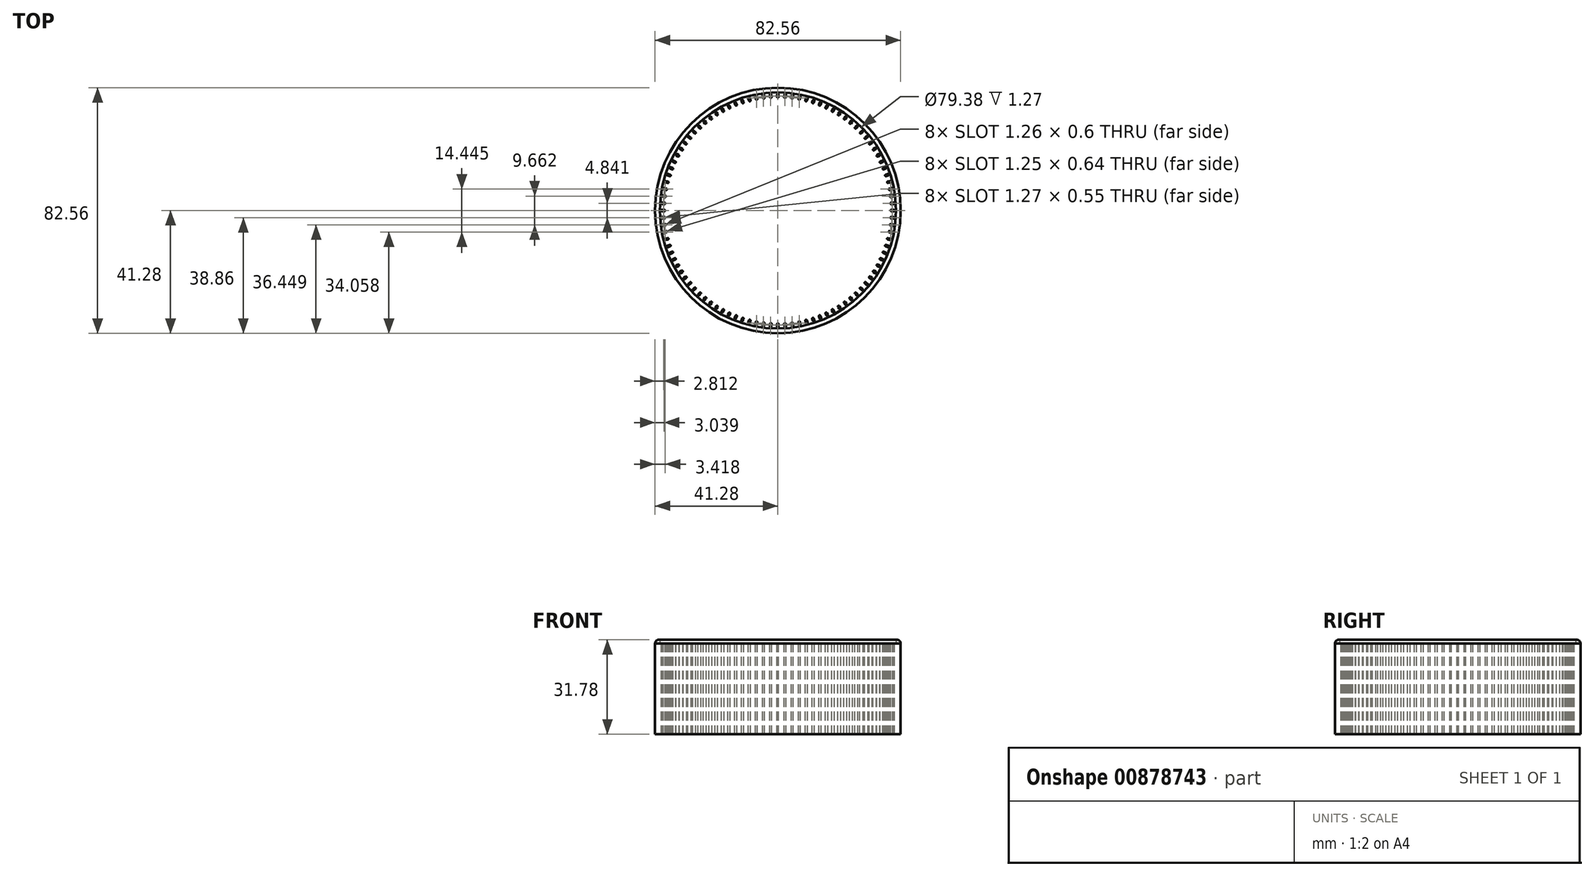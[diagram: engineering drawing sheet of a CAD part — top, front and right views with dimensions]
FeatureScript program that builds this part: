
annotation { "Feature Type Name" : "Feature", "Feature Type Description" : "" }
export const myFeature = defineFeature(function(context is Context, id is Id, definition is map)
    precondition{}
    {
        {
            var Q0;
            Q0=qCreatedBy(makeId("Top.planeOp"),FACE);
            var sketch = newSketch(context, id + "F0", { "sketchPlane" : qUnion([Q0])});
            skCircle(sketch, "E0", {"center": v(0, 0) * mm, "radius": 41.28 * mm});
            skSolve(sketch);
        }
        {
            var Q0;
            Q0 = qSketchRegion(id + "F0", true);
            extrude(context, id + "F1", {"entities" : qUnion([Q0]), "depth" : 30.48 * mm, "offsetDistance" : 25.4 * mm});
        }
        {
            var Q0;
            Q0=makeQuery(id+"F1.opExtrude","CAP_FACE",FACE,{"disambiguationData":[OSD([sQuery(id+"F0.wireOp",EDGE,"E0")])],"isStart":false});
            var sketch = newSketch(context, id + "F2", { "sketchPlane" : qUnion([Q0])});
            skCircle(sketch, "E1", {"center": v(0, 0) * mm, "radius": 39.69 * mm});
            skSolve(sketch);
        }
        {
            var Q0;
            Q0 = qSketchRegion(id + "F2", true);
            extrude(context, id + "F3", {"entities" : qUnion([Q0]), "operationType" : NewBodyOperationType.ADD, "depth" : 1.27 * mm, "offsetDistance" : 25.4 * mm});
        }
        {
            var Q0;
            Q0=qCreatedBy(makeId("Right.planeOp"),FACE);
            var sketch = newSketch(context, id + "F4", { "sketchPlane" : qUnion([Q0])});
            skLineSegment(sketch, "E2.0", {"start": v(-39.69, 31.75) * mm, "end": v(39.69, 31.75) * mm, "construction": true});
            skLineSegment(sketch, "E3.0", {"start": v(-41.28, 30.48) * mm, "end": v(41.28, 30.48) * mm, "construction": true});
            skArc(sketch, "E4", {"start": v(-39.69, 31.75) * mm, "mid": v(-40.79, 31.5) * mm, "end": v(-41.28, 30.48) * mm});
            skLineSegment(sketch, "E5", {"start": v(-39.69, 31.75) * mm, "end": v(-39.69, 30.48) * mm});
            skLineSegment(sketch, "E6", {"start": v(-39.69, 30.48) * mm, "end": v(-41.28, 30.48) * mm});
            skSolve(sketch);
        }
        {
            var Q0;
            Q0=qCreatedBy(makeId("Front.planeOp"),FACE);
            var sketch = newSketch(context, id + "F5", { "sketchPlane" : qUnion([Q0])});
            skLineSegment(sketch, "E7", {"start": v(0, 0) * mm, "end": v(0, 34.96) * mm});
            skSolve(sketch);
        }
        {
            var Q0;
            Q0 = qSketchRegion(id + "F4", true);
            var Q1;
            Q1=sQuery(id+"F5.wireOp",EDGE,"E7");
            revolve(context, id + "F6", {"surfaceOperationType" : NewSurfaceOperationType.NEW, "entities" : qUnion([Q0]), "axis" : qUnion([Q1]), "revolveType" : RevolveType.FULL});
        }
        {
            var Q0;
            Q0=makeQuery(id+"F3.opExtrude","CAP_FACE",FACE,{"disambiguationData":[OSD([sQuery(id+"F2.wireOp",EDGE,"E1")])],"isStart":false});
            var sketch = newSketch(context, id + "F7", { "sketchPlane" : qUnion([Q0])});
            skCircle(sketch, "E8", {"center": v(0, 0) * mm, "radius": 39.18 * mm, "construction": true});
            skLineSegment(sketch, "E9.bottom", {"start": v(-0.25, 38.93) * mm, "end": v(0.25, 38.93) * mm, "construction": true});
            skLineSegment(sketch, "E9.top", {"start": v(-0.25, 38.16) * mm, "end": v(0.25, 38.16) * mm, "construction": true});
            skLineSegment(sketch, "E9.left", {"start": v(-0.25, 38.93) * mm, "end": v(-0.25, 38.16) * mm});
            skLineSegment(sketch, "E9.right", {"start": v(0.25, 38.93) * mm, "end": v(0.25, 38.16) * mm});
            skArc(sketch, "E10", {"start": v(0.25, 38.93) * mm, "mid": v(0, 39.18) * mm, "end": v(-0.25, 38.93) * mm});
            skArc(sketch, "E11", {"start": v(-0.25, 38.16) * mm, "mid": v(0, 37.9) * mm, "end": v(0.25, 38.16) * mm});
            skArc(sketch, "E12.1.0", {"start": v(-2.2, 38.86) * mm, "mid": v(-2.46, 39.1) * mm, "end": v(-2.7, 38.83) * mm});
            skLineSegment(sketch, "E12.1.1", {"start": v(-2.2, 38.86) * mm, "end": v(-2.14, 38.1) * mm});
            skArc(sketch, "E12.1.2", {"start": v(-2.65, 38.07) * mm, "mid": v(-2.38, 37.83) * mm, "end": v(-2.14, 38.1) * mm});
            skLineSegment(sketch, "E12.1.3", {"start": v(-2.7, 38.83) * mm, "end": v(-2.65, 38.07) * mm});
            skArc(sketch, "E12.2.0", {"start": v(-4.63, 38.65) * mm, "mid": v(-4.91, 38.87) * mm, "end": v(-5.13, 38.59) * mm});
            skLineSegment(sketch, "E12.2.1", {"start": v(-4.63, 38.65) * mm, "end": v(-4.53, 37.9) * mm});
            skArc(sketch, "E12.2.2", {"start": v(-5.04, 37.83) * mm, "mid": v(-4.75, 37.61) * mm, "end": v(-4.53, 37.9) * mm});
            skLineSegment(sketch, "E12.2.3", {"start": v(-5.13, 38.59) * mm, "end": v(-5.04, 37.83) * mm});
            skArc(sketch, "E12.3.0", {"start": v(-7.04, 38.28) * mm, "mid": v(-7.34, 38.49) * mm, "end": v(-7.54, 38.19) * mm});
            skLineSegment(sketch, "E12.3.1", {"start": v(-7.04, 38.28) * mm, "end": v(-6.9, 37.54) * mm});
            skArc(sketch, "E12.3.2", {"start": v(-7.4, 37.44) * mm, "mid": v(-7.1, 37.24) * mm, "end": v(-6.9, 37.54) * mm});
            skLineSegment(sketch, "E12.3.3", {"start": v(-7.54, 38.19) * mm, "end": v(-7.4, 37.44) * mm});
            skArc(sketch, "E12.4.0", {"start": v(-9.43, 37.77) * mm, "mid": v(-9.74, 37.95) * mm, "end": v(-9.93, 37.64) * mm});
            skLineSegment(sketch, "E12.4.1", {"start": v(-9.43, 37.77) * mm, "end": v(-9.24, 37.03) * mm});
            skArc(sketch, "E12.4.2", {"start": v(-9.74, 36.9) * mm, "mid": v(-9.43, 36.72) * mm, "end": v(-9.24, 37.03) * mm});
            skLineSegment(sketch, "E12.4.3", {"start": v(-9.93, 37.64) * mm, "end": v(-9.74, 36.9) * mm});
            skArc(sketch, "E12.5.0", {"start": v(-11.79, 37.1) * mm, "mid": v(-12.1, 37.26) * mm, "end": v(-12.27, 36.94) * mm});
            skLineSegment(sketch, "E12.5.1", {"start": v(-11.79, 37.1) * mm, "end": v(-11.55, 36.37) * mm});
            skArc(sketch, "E12.5.2", {"start": v(-12.03, 36.22) * mm, "mid": v(-11.71, 36.05) * mm, "end": v(-11.55, 36.37) * mm});
            skLineSegment(sketch, "E12.5.3", {"start": v(-12.27, 36.94) * mm, "end": v(-12.03, 36.22) * mm});
            skArc(sketch, "E12.6.0", {"start": v(-14.1, 36.29) * mm, "mid": v(-14.42, 36.43) * mm, "end": v(-14.57, 36.1) * mm});
            skLineSegment(sketch, "E12.6.1", {"start": v(-14.1, 36.29) * mm, "end": v(-13.81, 35.58) * mm});
            skArc(sketch, "E12.6.2", {"start": v(-14.29, 35.4) * mm, "mid": v(-13.96, 35.25) * mm, "end": v(-13.81, 35.58) * mm});
            skLineSegment(sketch, "E12.6.3", {"start": v(-14.57, 36.1) * mm, "end": v(-14.29, 35.4) * mm});
            skArc(sketch, "E12.7.0", {"start": v(-16.34, 35.33) * mm, "mid": v(-16.68, 35.45) * mm, "end": v(-16.8, 35.11) * mm});
            skLineSegment(sketch, "E12.7.1", {"start": v(-16.34, 35.33) * mm, "end": v(-16.02, 34.64) * mm});
            skArc(sketch, "E12.7.2", {"start": v(-16.48, 34.42) * mm, "mid": v(-16.14, 34.3) * mm, "end": v(-16.02, 34.64) * mm});
            skLineSegment(sketch, "E12.7.3", {"start": v(-16.8, 35.11) * mm, "end": v(-16.48, 34.42) * mm});
            skArc(sketch, "E12.8.0", {"start": v(-18.53, 34.23) * mm, "mid": v(-18.87, 34.33) * mm, "end": v(-18.98, 33.99) * mm});
            skLineSegment(sketch, "E12.8.1", {"start": v(-18.53, 34.23) * mm, "end": v(-18.16, 33.57) * mm});
            skArc(sketch, "E12.8.2", {"start": v(-18.6, 33.32) * mm, "mid": v(-18.26, 33.22) * mm, "end": v(-18.16, 33.57) * mm});
            skLineSegment(sketch, "E12.8.3", {"start": v(-18.98, 33.99) * mm, "end": v(-18.6, 33.32) * mm});
            skArc(sketch, "E12.9.0", {"start": v(-20.64, 33) * mm, "mid": v(-21, 33.08) * mm, "end": v(-21.07, 32.73) * mm});
            skLineSegment(sketch, "E12.9.1", {"start": v(-20.64, 33) * mm, "end": v(-20.23, 32.36) * mm});
            skArc(sketch, "E12.9.2", {"start": v(-20.66, 32.09) * mm, "mid": v(-20.31, 32) * mm, "end": v(-20.23, 32.36) * mm});
            skLineSegment(sketch, "E12.9.3", {"start": v(-21.07, 32.73) * mm, "end": v(-20.66, 32.09) * mm});
            skArc(sketch, "E12.10.0", {"start": v(-22.67, 31.64) * mm, "mid": v(-23.03, 31.7) * mm, "end": v(-23.09, 31.34) * mm});
            skLineSegment(sketch, "E12.10.1", {"start": v(-22.67, 31.64) * mm, "end": v(-22.23, 31.02) * mm});
            skArc(sketch, "E12.10.2", {"start": v(-22.64, 30.73) * mm, "mid": v(-22.28, 30.67) * mm, "end": v(-22.23, 31.02) * mm});
            skLineSegment(sketch, "E12.10.3", {"start": v(-23.09, 31.34) * mm, "end": v(-22.64, 30.73) * mm});
            skArc(sketch, "E12.11.0", {"start": v(-24.62, 30.15) * mm, "mid": v(-24.97, 30.19) * mm, "end": v(-25, 29.83) * mm});
            skLineSegment(sketch, "E12.11.1", {"start": v(-24.62, 30.15) * mm, "end": v(-24.13, 29.57) * mm});
            skArc(sketch, "E12.11.2", {"start": v(-24.52, 29.24) * mm, "mid": v(-24.16, 29.2) * mm, "end": v(-24.13, 29.57) * mm});
            skLineSegment(sketch, "E12.11.3", {"start": v(-25, 29.83) * mm, "end": v(-24.52, 29.24) * mm});
            skArc(sketch, "E12.12.0", {"start": v(-26.46, 28.55) * mm, "mid": v(-26.82, 28.56) * mm, "end": v(-26.83, 28.2) * mm});
            skLineSegment(sketch, "E12.12.1", {"start": v(-26.46, 28.55) * mm, "end": v(-25.94, 28) * mm});
            skArc(sketch, "E12.12.2", {"start": v(-26.3, 27.65) * mm, "mid": v(-25.95, 27.63) * mm, "end": v(-25.94, 28) * mm});
            skLineSegment(sketch, "E12.12.3", {"start": v(-26.83, 28.2) * mm, "end": v(-26.3, 27.65) * mm});
            skArc(sketch, "E12.13.0", {"start": v(-28.2, 26.83) * mm, "mid": v(-28.56, 26.82) * mm, "end": v(-28.55, 26.46) * mm});
            skLineSegment(sketch, "E12.13.1", {"start": v(-28.2, 26.83) * mm, "end": v(-27.65, 26.3) * mm});
            skArc(sketch, "E12.13.2", {"start": v(-28, 25.94) * mm, "mid": v(-27.63, 25.95) * mm, "end": v(-27.65, 26.3) * mm});
            skLineSegment(sketch, "E12.13.3", {"start": v(-28.55, 26.46) * mm, "end": v(-28, 25.94) * mm});
            skArc(sketch, "E12.14.0", {"start": v(-29.83, 25) * mm, "mid": v(-30.19, 24.97) * mm, "end": v(-30.15, 24.62) * mm});
            skLineSegment(sketch, "E12.14.1", {"start": v(-29.83, 25) * mm, "end": v(-29.24, 24.52) * mm});
            skArc(sketch, "E12.14.2", {"start": v(-29.57, 24.13) * mm, "mid": v(-29.2, 24.16) * mm, "end": v(-29.24, 24.52) * mm});
            skLineSegment(sketch, "E12.14.3", {"start": v(-30.15, 24.62) * mm, "end": v(-29.57, 24.13) * mm});
            skArc(sketch, "E12.15.0", {"start": v(-31.34, 23.09) * mm, "mid": v(-31.7, 23.03) * mm, "end": v(-31.64, 22.67) * mm});
            skLineSegment(sketch, "E12.15.1", {"start": v(-31.34, 23.09) * mm, "end": v(-30.73, 22.64) * mm});
            skArc(sketch, "E12.15.2", {"start": v(-31.02, 22.23) * mm, "mid": v(-30.67, 22.28) * mm, "end": v(-30.73, 22.64) * mm});
            skLineSegment(sketch, "E12.15.3", {"start": v(-31.64, 22.67) * mm, "end": v(-31.02, 22.23) * mm});
            skArc(sketch, "E12.16.0", {"start": v(-32.73, 21.07) * mm, "mid": v(-33.08, 21) * mm, "end": v(-33, 20.64) * mm});
            skLineSegment(sketch, "E12.16.1", {"start": v(-32.73, 21.07) * mm, "end": v(-32.09, 20.66) * mm});
            skArc(sketch, "E12.16.2", {"start": v(-32.36, 20.23) * mm, "mid": v(-32, 20.31) * mm, "end": v(-32.09, 20.66) * mm});
            skLineSegment(sketch, "E12.16.3", {"start": v(-33, 20.64) * mm, "end": v(-32.36, 20.23) * mm});
            skArc(sketch, "E12.17.0", {"start": v(-33.99, 18.98) * mm, "mid": v(-34.33, 18.87) * mm, "end": v(-34.23, 18.53) * mm});
            skLineSegment(sketch, "E12.17.1", {"start": v(-33.99, 18.98) * mm, "end": v(-33.32, 18.6) * mm});
            skArc(sketch, "E12.17.2", {"start": v(-33.57, 18.16) * mm, "mid": v(-33.22, 18.26) * mm, "end": v(-33.32, 18.6) * mm});
            skLineSegment(sketch, "E12.17.3", {"start": v(-34.23, 18.53) * mm, "end": v(-33.57, 18.16) * mm});
            skArc(sketch, "E12.18.0", {"start": v(-35.11, 16.8) * mm, "mid": v(-35.45, 16.68) * mm, "end": v(-35.33, 16.34) * mm});
            skLineSegment(sketch, "E12.18.1", {"start": v(-35.11, 16.8) * mm, "end": v(-34.42, 16.48) * mm});
            skArc(sketch, "E12.18.2", {"start": v(-34.64, 16.02) * mm, "mid": v(-34.3, 16.14) * mm, "end": v(-34.42, 16.48) * mm});
            skLineSegment(sketch, "E12.18.3", {"start": v(-35.33, 16.34) * mm, "end": v(-34.64, 16.02) * mm});
            skArc(sketch, "E12.19.0", {"start": v(-36.1, 14.57) * mm, "mid": v(-36.43, 14.42) * mm, "end": v(-36.29, 14.1) * mm});
            skLineSegment(sketch, "E12.19.1", {"start": v(-36.1, 14.57) * mm, "end": v(-35.4, 14.29) * mm});
            skArc(sketch, "E12.19.2", {"start": v(-35.58, 13.81) * mm, "mid": v(-35.25, 13.96) * mm, "end": v(-35.4, 14.29) * mm});
            skLineSegment(sketch, "E12.19.3", {"start": v(-36.29, 14.1) * mm, "end": v(-35.58, 13.81) * mm});
            skArc(sketch, "E12.20.0", {"start": v(-36.94, 12.27) * mm, "mid": v(-37.26, 12.1) * mm, "end": v(-37.1, 11.79) * mm});
            skLineSegment(sketch, "E12.20.1", {"start": v(-36.94, 12.27) * mm, "end": v(-36.22, 12.03) * mm});
            skArc(sketch, "E12.20.2", {"start": v(-36.37, 11.55) * mm, "mid": v(-36.05, 11.71) * mm, "end": v(-36.22, 12.03) * mm});
            skLineSegment(sketch, "E12.20.3", {"start": v(-37.1, 11.79) * mm, "end": v(-36.37, 11.55) * mm});
            skArc(sketch, "E12.21.0", {"start": v(-37.64, 9.93) * mm, "mid": v(-37.95, 9.74) * mm, "end": v(-37.77, 9.43) * mm});
            skLineSegment(sketch, "E12.21.1", {"start": v(-37.64, 9.93) * mm, "end": v(-36.9, 9.74) * mm});
            skArc(sketch, "E12.21.2", {"start": v(-37.03, 9.24) * mm, "mid": v(-36.72, 9.43) * mm, "end": v(-36.9, 9.74) * mm});
            skLineSegment(sketch, "E12.21.3", {"start": v(-37.77, 9.43) * mm, "end": v(-37.03, 9.24) * mm});
            skArc(sketch, "E12.22.0", {"start": v(-38.19, 7.54) * mm, "mid": v(-38.49, 7.34) * mm, "end": v(-38.28, 7.04) * mm});
            skLineSegment(sketch, "E12.22.1", {"start": v(-38.19, 7.54) * mm, "end": v(-37.44, 7.4) * mm});
            skArc(sketch, "E12.22.2", {"start": v(-37.54, 6.9) * mm, "mid": v(-37.24, 7.1) * mm, "end": v(-37.44, 7.4) * mm});
            skLineSegment(sketch, "E12.22.3", {"start": v(-38.28, 7.04) * mm, "end": v(-37.54, 6.9) * mm});
            skArc(sketch, "E12.23.0", {"start": v(-38.59, 5.13) * mm, "mid": v(-38.87, 4.91) * mm, "end": v(-38.65, 4.63) * mm});
            skLineSegment(sketch, "E12.23.1", {"start": v(-38.59, 5.13) * mm, "end": v(-37.83, 5.04) * mm});
            skArc(sketch, "E12.23.2", {"start": v(-37.9, 4.53) * mm, "mid": v(-37.61, 4.75) * mm, "end": v(-37.83, 5.04) * mm});
            skLineSegment(sketch, "E12.23.3", {"start": v(-38.65, 4.63) * mm, "end": v(-37.9, 4.53) * mm});
            skArc(sketch, "E12.24.0", {"start": v(-38.83, 2.7) * mm, "mid": v(-39.1, 2.46) * mm, "end": v(-38.86, 2.2) * mm});
            skLineSegment(sketch, "E12.24.1", {"start": v(-38.83, 2.7) * mm, "end": v(-38.07, 2.65) * mm});
            skArc(sketch, "E12.24.2", {"start": v(-38.1, 2.14) * mm, "mid": v(-37.83, 2.38) * mm, "end": v(-38.07, 2.65) * mm});
            skLineSegment(sketch, "E12.24.3", {"start": v(-38.86, 2.2) * mm, "end": v(-38.1, 2.14) * mm});
            skArc(sketch, "E12.25.0", {"start": v(-38.93, 0.25) * mm, "mid": v(-39.18, 0) * mm, "end": v(-38.93, -0.25) * mm});
            skLineSegment(sketch, "E12.25.1", {"start": v(-38.93, 0.25) * mm, "end": v(-38.16, 0.25) * mm});
            skArc(sketch, "E12.25.2", {"start": v(-38.16, -0.25) * mm, "mid": v(-37.9, 0) * mm, "end": v(-38.16, 0.25) * mm});
            skLineSegment(sketch, "E12.25.3", {"start": v(-38.93, -0.25) * mm, "end": v(-38.16, -0.25) * mm});
            skArc(sketch, "E12.26.0", {"start": v(-38.86, -2.2) * mm, "mid": v(-39.1, -2.46) * mm, "end": v(-38.83, -2.7) * mm});
            skLineSegment(sketch, "E12.26.1", {"start": v(-38.86, -2.2) * mm, "end": v(-38.1, -2.14) * mm});
            skArc(sketch, "E12.26.2", {"start": v(-38.07, -2.65) * mm, "mid": v(-37.83, -2.38) * mm, "end": v(-38.1, -2.14) * mm});
            skLineSegment(sketch, "E12.26.3", {"start": v(-38.83, -2.7) * mm, "end": v(-38.07, -2.65) * mm});
            skArc(sketch, "E12.27.0", {"start": v(-38.65, -4.63) * mm, "mid": v(-38.87, -4.91) * mm, "end": v(-38.59, -5.13) * mm});
            skLineSegment(sketch, "E12.27.1", {"start": v(-38.65, -4.63) * mm, "end": v(-37.9, -4.53) * mm});
            skArc(sketch, "E12.27.2", {"start": v(-37.83, -5.04) * mm, "mid": v(-37.61, -4.75) * mm, "end": v(-37.9, -4.53) * mm});
            skLineSegment(sketch, "E12.27.3", {"start": v(-38.59, -5.13) * mm, "end": v(-37.83, -5.04) * mm});
            skArc(sketch, "E12.28.0", {"start": v(-38.28, -7.04) * mm, "mid": v(-38.49, -7.34) * mm, "end": v(-38.19, -7.54) * mm});
            skLineSegment(sketch, "E12.28.1", {"start": v(-38.28, -7.04) * mm, "end": v(-37.54, -6.9) * mm});
            skArc(sketch, "E12.28.2", {"start": v(-37.44, -7.4) * mm, "mid": v(-37.24, -7.1) * mm, "end": v(-37.54, -6.9) * mm});
            skLineSegment(sketch, "E12.28.3", {"start": v(-38.19, -7.54) * mm, "end": v(-37.44, -7.4) * mm});
            skArc(sketch, "E12.29.0", {"start": v(-37.77, -9.43) * mm, "mid": v(-37.95, -9.74) * mm, "end": v(-37.64, -9.93) * mm});
            skLineSegment(sketch, "E12.29.1", {"start": v(-37.77, -9.43) * mm, "end": v(-37.03, -9.24) * mm});
            skArc(sketch, "E12.29.2", {"start": v(-36.9, -9.74) * mm, "mid": v(-36.72, -9.43) * mm, "end": v(-37.03, -9.24) * mm});
            skLineSegment(sketch, "E12.29.3", {"start": v(-37.64, -9.93) * mm, "end": v(-36.9, -9.74) * mm});
            skArc(sketch, "E12.30.0", {"start": v(-37.1, -11.79) * mm, "mid": v(-37.26, -12.1) * mm, "end": v(-36.94, -12.27) * mm});
            skLineSegment(sketch, "E12.30.1", {"start": v(-37.1, -11.79) * mm, "end": v(-36.37, -11.55) * mm});
            skArc(sketch, "E12.30.2", {"start": v(-36.22, -12.03) * mm, "mid": v(-36.05, -11.71) * mm, "end": v(-36.37, -11.55) * mm});
            skLineSegment(sketch, "E12.30.3", {"start": v(-36.94, -12.27) * mm, "end": v(-36.22, -12.03) * mm});
            skArc(sketch, "E12.31.0", {"start": v(-36.29, -14.1) * mm, "mid": v(-36.43, -14.42) * mm, "end": v(-36.1, -14.57) * mm});
            skLineSegment(sketch, "E12.31.1", {"start": v(-36.29, -14.1) * mm, "end": v(-35.58, -13.81) * mm});
            skArc(sketch, "E12.31.2", {"start": v(-35.4, -14.29) * mm, "mid": v(-35.25, -13.96) * mm, "end": v(-35.58, -13.81) * mm});
            skLineSegment(sketch, "E12.31.3", {"start": v(-36.1, -14.57) * mm, "end": v(-35.4, -14.29) * mm});
            skArc(sketch, "E12.32.0", {"start": v(-35.33, -16.34) * mm, "mid": v(-35.45, -16.68) * mm, "end": v(-35.11, -16.8) * mm});
            skLineSegment(sketch, "E12.32.1", {"start": v(-35.33, -16.34) * mm, "end": v(-34.64, -16.02) * mm});
            skArc(sketch, "E12.32.2", {"start": v(-34.42, -16.48) * mm, "mid": v(-34.3, -16.14) * mm, "end": v(-34.64, -16.02) * mm});
            skLineSegment(sketch, "E12.32.3", {"start": v(-35.11, -16.8) * mm, "end": v(-34.42, -16.48) * mm});
            skArc(sketch, "E12.33.0", {"start": v(-34.23, -18.53) * mm, "mid": v(-34.33, -18.87) * mm, "end": v(-33.99, -18.98) * mm});
            skLineSegment(sketch, "E12.33.1", {"start": v(-34.23, -18.53) * mm, "end": v(-33.57, -18.16) * mm});
            skArc(sketch, "E12.33.2", {"start": v(-33.32, -18.6) * mm, "mid": v(-33.22, -18.26) * mm, "end": v(-33.57, -18.16) * mm});
            skLineSegment(sketch, "E12.33.3", {"start": v(-33.99, -18.98) * mm, "end": v(-33.32, -18.6) * mm});
            skArc(sketch, "E12.34.0", {"start": v(-33, -20.64) * mm, "mid": v(-33.08, -21) * mm, "end": v(-32.73, -21.07) * mm});
            skLineSegment(sketch, "E12.34.1", {"start": v(-33, -20.64) * mm, "end": v(-32.36, -20.23) * mm});
            skArc(sketch, "E12.34.2", {"start": v(-32.09, -20.66) * mm, "mid": v(-32, -20.31) * mm, "end": v(-32.36, -20.23) * mm});
            skLineSegment(sketch, "E12.34.3", {"start": v(-32.73, -21.07) * mm, "end": v(-32.09, -20.66) * mm});
            skArc(sketch, "E12.35.0", {"start": v(-31.64, -22.67) * mm, "mid": v(-31.7, -23.03) * mm, "end": v(-31.34, -23.09) * mm});
            skLineSegment(sketch, "E12.35.1", {"start": v(-31.64, -22.67) * mm, "end": v(-31.02, -22.23) * mm});
            skArc(sketch, "E12.35.2", {"start": v(-30.73, -22.64) * mm, "mid": v(-30.67, -22.28) * mm, "end": v(-31.02, -22.23) * mm});
            skLineSegment(sketch, "E12.35.3", {"start": v(-31.34, -23.09) * mm, "end": v(-30.73, -22.64) * mm});
            skArc(sketch, "E12.36.0", {"start": v(-30.15, -24.62) * mm, "mid": v(-30.19, -24.97) * mm, "end": v(-29.83, -25) * mm});
            skLineSegment(sketch, "E12.36.1", {"start": v(-30.15, -24.62) * mm, "end": v(-29.57, -24.13) * mm});
            skArc(sketch, "E12.36.2", {"start": v(-29.24, -24.52) * mm, "mid": v(-29.2, -24.16) * mm, "end": v(-29.57, -24.13) * mm});
            skLineSegment(sketch, "E12.36.3", {"start": v(-29.83, -25) * mm, "end": v(-29.24, -24.52) * mm});
            skArc(sketch, "E12.37.0", {"start": v(-28.55, -26.46) * mm, "mid": v(-28.56, -26.82) * mm, "end": v(-28.2, -26.83) * mm});
            skLineSegment(sketch, "E12.37.1", {"start": v(-28.55, -26.46) * mm, "end": v(-28, -25.94) * mm});
            skArc(sketch, "E12.37.2", {"start": v(-27.65, -26.3) * mm, "mid": v(-27.63, -25.95) * mm, "end": v(-28, -25.94) * mm});
            skLineSegment(sketch, "E12.37.3", {"start": v(-28.2, -26.83) * mm, "end": v(-27.65, -26.3) * mm});
            skArc(sketch, "E12.38.0", {"start": v(-26.83, -28.2) * mm, "mid": v(-26.82, -28.56) * mm, "end": v(-26.46, -28.55) * mm});
            skLineSegment(sketch, "E12.38.1", {"start": v(-26.83, -28.2) * mm, "end": v(-26.3, -27.65) * mm});
            skArc(sketch, "E12.38.2", {"start": v(-25.94, -28) * mm, "mid": v(-25.95, -27.63) * mm, "end": v(-26.3, -27.65) * mm});
            skLineSegment(sketch, "E12.38.3", {"start": v(-26.46, -28.55) * mm, "end": v(-25.94, -28) * mm});
            skArc(sketch, "E12.39.0", {"start": v(-25, -29.83) * mm, "mid": v(-24.97, -30.19) * mm, "end": v(-24.62, -30.15) * mm});
            skLineSegment(sketch, "E12.39.1", {"start": v(-25, -29.83) * mm, "end": v(-24.52, -29.24) * mm});
            skArc(sketch, "E12.39.2", {"start": v(-24.13, -29.57) * mm, "mid": v(-24.16, -29.2) * mm, "end": v(-24.52, -29.24) * mm});
            skLineSegment(sketch, "E12.39.3", {"start": v(-24.62, -30.15) * mm, "end": v(-24.13, -29.57) * mm});
            skArc(sketch, "E12.40.0", {"start": v(-23.09, -31.34) * mm, "mid": v(-23.03, -31.7) * mm, "end": v(-22.67, -31.64) * mm});
            skLineSegment(sketch, "E12.40.1", {"start": v(-23.09, -31.34) * mm, "end": v(-22.64, -30.73) * mm});
            skArc(sketch, "E12.40.2", {"start": v(-22.23, -31.02) * mm, "mid": v(-22.28, -30.67) * mm, "end": v(-22.64, -30.73) * mm});
            skLineSegment(sketch, "E12.40.3", {"start": v(-22.67, -31.64) * mm, "end": v(-22.23, -31.02) * mm});
            skArc(sketch, "E12.41.0", {"start": v(-21.07, -32.73) * mm, "mid": v(-21, -33.08) * mm, "end": v(-20.64, -33) * mm});
            skLineSegment(sketch, "E12.41.1", {"start": v(-21.07, -32.73) * mm, "end": v(-20.66, -32.09) * mm});
            skArc(sketch, "E12.41.2", {"start": v(-20.23, -32.36) * mm, "mid": v(-20.31, -32) * mm, "end": v(-20.66, -32.09) * mm});
            skLineSegment(sketch, "E12.41.3", {"start": v(-20.64, -33) * mm, "end": v(-20.23, -32.36) * mm});
            skArc(sketch, "E12.42.0", {"start": v(-18.98, -33.99) * mm, "mid": v(-18.87, -34.33) * mm, "end": v(-18.53, -34.23) * mm});
            skLineSegment(sketch, "E12.42.1", {"start": v(-18.98, -33.99) * mm, "end": v(-18.6, -33.32) * mm});
            skArc(sketch, "E12.42.2", {"start": v(-18.16, -33.57) * mm, "mid": v(-18.26, -33.22) * mm, "end": v(-18.6, -33.32) * mm});
            skLineSegment(sketch, "E12.42.3", {"start": v(-18.53, -34.23) * mm, "end": v(-18.16, -33.57) * mm});
            skArc(sketch, "E12.43.0", {"start": v(-16.8, -35.11) * mm, "mid": v(-16.68, -35.45) * mm, "end": v(-16.34, -35.33) * mm});
            skLineSegment(sketch, "E12.43.1", {"start": v(-16.8, -35.11) * mm, "end": v(-16.48, -34.42) * mm});
            skArc(sketch, "E12.43.2", {"start": v(-16.02, -34.64) * mm, "mid": v(-16.14, -34.3) * mm, "end": v(-16.48, -34.42) * mm});
            skLineSegment(sketch, "E12.43.3", {"start": v(-16.34, -35.33) * mm, "end": v(-16.02, -34.64) * mm});
            skArc(sketch, "E12.44.0", {"start": v(-14.57, -36.1) * mm, "mid": v(-14.42, -36.43) * mm, "end": v(-14.1, -36.29) * mm});
            skLineSegment(sketch, "E12.44.1", {"start": v(-14.57, -36.1) * mm, "end": v(-14.29, -35.4) * mm});
            skArc(sketch, "E12.44.2", {"start": v(-13.81, -35.58) * mm, "mid": v(-13.96, -35.25) * mm, "end": v(-14.29, -35.4) * mm});
            skLineSegment(sketch, "E12.44.3", {"start": v(-14.1, -36.29) * mm, "end": v(-13.81, -35.58) * mm});
            skArc(sketch, "E12.45.0", {"start": v(-12.27, -36.94) * mm, "mid": v(-12.1, -37.26) * mm, "end": v(-11.79, -37.1) * mm});
            skLineSegment(sketch, "E12.45.1", {"start": v(-12.27, -36.94) * mm, "end": v(-12.03, -36.22) * mm});
            skArc(sketch, "E12.45.2", {"start": v(-11.55, -36.37) * mm, "mid": v(-11.71, -36.05) * mm, "end": v(-12.03, -36.22) * mm});
            skLineSegment(sketch, "E12.45.3", {"start": v(-11.79, -37.1) * mm, "end": v(-11.55, -36.37) * mm});
            skArc(sketch, "E12.46.0", {"start": v(-9.93, -37.64) * mm, "mid": v(-9.74, -37.95) * mm, "end": v(-9.43, -37.77) * mm});
            skLineSegment(sketch, "E12.46.1", {"start": v(-9.93, -37.64) * mm, "end": v(-9.74, -36.9) * mm});
            skArc(sketch, "E12.46.2", {"start": v(-9.24, -37.03) * mm, "mid": v(-9.43, -36.72) * mm, "end": v(-9.74, -36.9) * mm});
            skLineSegment(sketch, "E12.46.3", {"start": v(-9.43, -37.77) * mm, "end": v(-9.24, -37.03) * mm});
            skArc(sketch, "E12.47.0", {"start": v(-7.54, -38.19) * mm, "mid": v(-7.34, -38.49) * mm, "end": v(-7.04, -38.28) * mm});
            skLineSegment(sketch, "E12.47.1", {"start": v(-7.54, -38.19) * mm, "end": v(-7.4, -37.44) * mm});
            skArc(sketch, "E12.47.2", {"start": v(-6.9, -37.54) * mm, "mid": v(-7.1, -37.24) * mm, "end": v(-7.4, -37.44) * mm});
            skLineSegment(sketch, "E12.47.3", {"start": v(-7.04, -38.28) * mm, "end": v(-6.9, -37.54) * mm});
            skArc(sketch, "E12.48.0", {"start": v(-5.13, -38.59) * mm, "mid": v(-4.91, -38.87) * mm, "end": v(-4.63, -38.65) * mm});
            skLineSegment(sketch, "E12.48.1", {"start": v(-5.13, -38.59) * mm, "end": v(-5.04, -37.83) * mm});
            skArc(sketch, "E12.48.2", {"start": v(-4.53, -37.9) * mm, "mid": v(-4.75, -37.61) * mm, "end": v(-5.04, -37.83) * mm});
            skLineSegment(sketch, "E12.48.3", {"start": v(-4.63, -38.65) * mm, "end": v(-4.53, -37.9) * mm});
            skArc(sketch, "E12.49.0", {"start": v(-2.7, -38.83) * mm, "mid": v(-2.46, -39.1) * mm, "end": v(-2.2, -38.86) * mm});
            skLineSegment(sketch, "E12.49.1", {"start": v(-2.7, -38.83) * mm, "end": v(-2.65, -38.07) * mm});
            skArc(sketch, "E12.49.2", {"start": v(-2.14, -38.1) * mm, "mid": v(-2.38, -37.83) * mm, "end": v(-2.65, -38.07) * mm});
            skLineSegment(sketch, "E12.49.3", {"start": v(-2.2, -38.86) * mm, "end": v(-2.14, -38.1) * mm});
            skArc(sketch, "E12.50.0", {"start": v(-0.25, -38.93) * mm, "mid": v(0, -39.18) * mm, "end": v(0.25, -38.93) * mm});
            skLineSegment(sketch, "E12.50.1", {"start": v(-0.25, -38.93) * mm, "end": v(-0.25, -38.16) * mm});
            skArc(sketch, "E12.50.2", {"start": v(0.25, -38.16) * mm, "mid": v(0, -37.9) * mm, "end": v(-0.25, -38.16) * mm});
            skLineSegment(sketch, "E12.50.3", {"start": v(0.25, -38.93) * mm, "end": v(0.25, -38.16) * mm});
            skArc(sketch, "E12.51.0", {"start": v(2.2, -38.86) * mm, "mid": v(2.46, -39.1) * mm, "end": v(2.7, -38.83) * mm});
            skLineSegment(sketch, "E12.51.1", {"start": v(2.2, -38.86) * mm, "end": v(2.14, -38.1) * mm});
            skArc(sketch, "E12.51.2", {"start": v(2.65, -38.07) * mm, "mid": v(2.38, -37.83) * mm, "end": v(2.14, -38.1) * mm});
            skLineSegment(sketch, "E12.51.3", {"start": v(2.7, -38.83) * mm, "end": v(2.65, -38.07) * mm});
            skArc(sketch, "E12.52.0", {"start": v(4.63, -38.65) * mm, "mid": v(4.91, -38.87) * mm, "end": v(5.13, -38.59) * mm});
            skLineSegment(sketch, "E12.52.1", {"start": v(4.63, -38.65) * mm, "end": v(4.53, -37.9) * mm});
            skArc(sketch, "E12.52.2", {"start": v(5.04, -37.83) * mm, "mid": v(4.75, -37.61) * mm, "end": v(4.53, -37.9) * mm});
            skLineSegment(sketch, "E12.52.3", {"start": v(5.13, -38.59) * mm, "end": v(5.04, -37.83) * mm});
            skArc(sketch, "E12.53.0", {"start": v(7.04, -38.28) * mm, "mid": v(7.34, -38.49) * mm, "end": v(7.54, -38.19) * mm});
            skLineSegment(sketch, "E12.53.1", {"start": v(7.04, -38.28) * mm, "end": v(6.9, -37.54) * mm});
            skArc(sketch, "E12.53.2", {"start": v(7.4, -37.44) * mm, "mid": v(7.1, -37.24) * mm, "end": v(6.9, -37.54) * mm});
            skLineSegment(sketch, "E12.53.3", {"start": v(7.54, -38.19) * mm, "end": v(7.4, -37.44) * mm});
            skArc(sketch, "E12.54.0", {"start": v(9.43, -37.77) * mm, "mid": v(9.74, -37.95) * mm, "end": v(9.93, -37.64) * mm});
            skLineSegment(sketch, "E12.54.1", {"start": v(9.43, -37.77) * mm, "end": v(9.24, -37.03) * mm});
            skArc(sketch, "E12.54.2", {"start": v(9.74, -36.9) * mm, "mid": v(9.43, -36.72) * mm, "end": v(9.24, -37.03) * mm});
            skLineSegment(sketch, "E12.54.3", {"start": v(9.93, -37.64) * mm, "end": v(9.74, -36.9) * mm});
            skArc(sketch, "E12.55.0", {"start": v(11.79, -37.1) * mm, "mid": v(12.1, -37.26) * mm, "end": v(12.27, -36.94) * mm});
            skLineSegment(sketch, "E12.55.1", {"start": v(11.79, -37.1) * mm, "end": v(11.55, -36.37) * mm});
            skArc(sketch, "E12.55.2", {"start": v(12.03, -36.22) * mm, "mid": v(11.71, -36.05) * mm, "end": v(11.55, -36.37) * mm});
            skLineSegment(sketch, "E12.55.3", {"start": v(12.27, -36.94) * mm, "end": v(12.03, -36.22) * mm});
            skArc(sketch, "E12.56.0", {"start": v(14.1, -36.29) * mm, "mid": v(14.42, -36.43) * mm, "end": v(14.57, -36.1) * mm});
            skLineSegment(sketch, "E12.56.1", {"start": v(14.1, -36.29) * mm, "end": v(13.81, -35.58) * mm});
            skArc(sketch, "E12.56.2", {"start": v(14.29, -35.4) * mm, "mid": v(13.96, -35.25) * mm, "end": v(13.81, -35.58) * mm});
            skLineSegment(sketch, "E12.56.3", {"start": v(14.57, -36.1) * mm, "end": v(14.29, -35.4) * mm});
            skArc(sketch, "E12.57.0", {"start": v(16.34, -35.33) * mm, "mid": v(16.68, -35.45) * mm, "end": v(16.8, -35.11) * mm});
            skLineSegment(sketch, "E12.57.1", {"start": v(16.34, -35.33) * mm, "end": v(16.02, -34.64) * mm});
            skArc(sketch, "E12.57.2", {"start": v(16.48, -34.42) * mm, "mid": v(16.14, -34.3) * mm, "end": v(16.02, -34.64) * mm});
            skLineSegment(sketch, "E12.57.3", {"start": v(16.8, -35.11) * mm, "end": v(16.48, -34.42) * mm});
            skArc(sketch, "E12.58.0", {"start": v(18.53, -34.23) * mm, "mid": v(18.87, -34.33) * mm, "end": v(18.98, -33.99) * mm});
            skLineSegment(sketch, "E12.58.1", {"start": v(18.53, -34.23) * mm, "end": v(18.16, -33.57) * mm});
            skArc(sketch, "E12.58.2", {"start": v(18.6, -33.32) * mm, "mid": v(18.26, -33.22) * mm, "end": v(18.16, -33.57) * mm});
            skLineSegment(sketch, "E12.58.3", {"start": v(18.98, -33.99) * mm, "end": v(18.6, -33.32) * mm});
            skArc(sketch, "E12.59.0", {"start": v(20.64, -33) * mm, "mid": v(21, -33.08) * mm, "end": v(21.07, -32.73) * mm});
            skLineSegment(sketch, "E12.59.1", {"start": v(20.64, -33) * mm, "end": v(20.23, -32.36) * mm});
            skArc(sketch, "E12.59.2", {"start": v(20.66, -32.09) * mm, "mid": v(20.31, -32) * mm, "end": v(20.23, -32.36) * mm});
            skLineSegment(sketch, "E12.59.3", {"start": v(21.07, -32.73) * mm, "end": v(20.66, -32.09) * mm});
            skArc(sketch, "E12.60.0", {"start": v(22.67, -31.64) * mm, "mid": v(23.03, -31.7) * mm, "end": v(23.09, -31.34) * mm});
            skLineSegment(sketch, "E12.60.1", {"start": v(22.67, -31.64) * mm, "end": v(22.23, -31.02) * mm});
            skArc(sketch, "E12.60.2", {"start": v(22.64, -30.73) * mm, "mid": v(22.28, -30.67) * mm, "end": v(22.23, -31.02) * mm});
            skLineSegment(sketch, "E12.60.3", {"start": v(23.09, -31.34) * mm, "end": v(22.64, -30.73) * mm});
            skArc(sketch, "E12.61.0", {"start": v(24.62, -30.15) * mm, "mid": v(24.97, -30.19) * mm, "end": v(25, -29.83) * mm});
            skLineSegment(sketch, "E12.61.1", {"start": v(24.62, -30.15) * mm, "end": v(24.13, -29.57) * mm});
            skArc(sketch, "E12.61.2", {"start": v(24.52, -29.24) * mm, "mid": v(24.16, -29.2) * mm, "end": v(24.13, -29.57) * mm});
            skLineSegment(sketch, "E12.61.3", {"start": v(25, -29.83) * mm, "end": v(24.52, -29.24) * mm});
            skArc(sketch, "E12.62.0", {"start": v(26.46, -28.55) * mm, "mid": v(26.82, -28.56) * mm, "end": v(26.83, -28.2) * mm});
            skLineSegment(sketch, "E12.62.1", {"start": v(26.46, -28.55) * mm, "end": v(25.94, -28) * mm});
            skArc(sketch, "E12.62.2", {"start": v(26.3, -27.65) * mm, "mid": v(25.95, -27.63) * mm, "end": v(25.94, -28) * mm});
            skLineSegment(sketch, "E12.62.3", {"start": v(26.83, -28.2) * mm, "end": v(26.3, -27.65) * mm});
            skArc(sketch, "E12.63.0", {"start": v(28.2, -26.83) * mm, "mid": v(28.56, -26.82) * mm, "end": v(28.55, -26.46) * mm});
            skLineSegment(sketch, "E12.63.1", {"start": v(28.2, -26.83) * mm, "end": v(27.65, -26.3) * mm});
            skArc(sketch, "E12.63.2", {"start": v(28, -25.94) * mm, "mid": v(27.63, -25.95) * mm, "end": v(27.65, -26.3) * mm});
            skLineSegment(sketch, "E12.63.3", {"start": v(28.55, -26.46) * mm, "end": v(28, -25.94) * mm});
            skArc(sketch, "E12.64.0", {"start": v(29.83, -25) * mm, "mid": v(30.19, -24.97) * mm, "end": v(30.15, -24.62) * mm});
            skLineSegment(sketch, "E12.64.1", {"start": v(29.83, -25) * mm, "end": v(29.24, -24.52) * mm});
            skArc(sketch, "E12.64.2", {"start": v(29.57, -24.13) * mm, "mid": v(29.2, -24.16) * mm, "end": v(29.24, -24.52) * mm});
            skLineSegment(sketch, "E12.64.3", {"start": v(30.15, -24.62) * mm, "end": v(29.57, -24.13) * mm});
            skArc(sketch, "E12.65.0", {"start": v(31.34, -23.09) * mm, "mid": v(31.7, -23.03) * mm, "end": v(31.64, -22.67) * mm});
            skLineSegment(sketch, "E12.65.1", {"start": v(31.34, -23.09) * mm, "end": v(30.73, -22.64) * mm});
            skArc(sketch, "E12.65.2", {"start": v(31.02, -22.23) * mm, "mid": v(30.67, -22.28) * mm, "end": v(30.73, -22.64) * mm});
            skLineSegment(sketch, "E12.65.3", {"start": v(31.64, -22.67) * mm, "end": v(31.02, -22.23) * mm});
            skArc(sketch, "E12.66.0", {"start": v(32.73, -21.07) * mm, "mid": v(33.08, -21) * mm, "end": v(33, -20.64) * mm});
            skLineSegment(sketch, "E12.66.1", {"start": v(32.73, -21.07) * mm, "end": v(32.09, -20.66) * mm});
            skArc(sketch, "E12.66.2", {"start": v(32.36, -20.23) * mm, "mid": v(32, -20.31) * mm, "end": v(32.09, -20.66) * mm});
            skLineSegment(sketch, "E12.66.3", {"start": v(33, -20.64) * mm, "end": v(32.36, -20.23) * mm});
            skArc(sketch, "E12.67.0", {"start": v(33.99, -18.98) * mm, "mid": v(34.33, -18.87) * mm, "end": v(34.23, -18.53) * mm});
            skLineSegment(sketch, "E12.67.1", {"start": v(33.99, -18.98) * mm, "end": v(33.32, -18.6) * mm});
            skArc(sketch, "E12.67.2", {"start": v(33.57, -18.16) * mm, "mid": v(33.22, -18.26) * mm, "end": v(33.32, -18.6) * mm});
            skLineSegment(sketch, "E12.67.3", {"start": v(34.23, -18.53) * mm, "end": v(33.57, -18.16) * mm});
            skArc(sketch, "E12.68.0", {"start": v(35.11, -16.8) * mm, "mid": v(35.45, -16.68) * mm, "end": v(35.33, -16.34) * mm});
            skLineSegment(sketch, "E12.68.1", {"start": v(35.11, -16.8) * mm, "end": v(34.42, -16.48) * mm});
            skArc(sketch, "E12.68.2", {"start": v(34.64, -16.02) * mm, "mid": v(34.3, -16.14) * mm, "end": v(34.42, -16.48) * mm});
            skLineSegment(sketch, "E12.68.3", {"start": v(35.33, -16.34) * mm, "end": v(34.64, -16.02) * mm});
            skArc(sketch, "E12.69.0", {"start": v(36.1, -14.57) * mm, "mid": v(36.43, -14.42) * mm, "end": v(36.29, -14.1) * mm});
            skLineSegment(sketch, "E12.69.1", {"start": v(36.1, -14.57) * mm, "end": v(35.4, -14.29) * mm});
            skArc(sketch, "E12.69.2", {"start": v(35.58, -13.81) * mm, "mid": v(35.25, -13.96) * mm, "end": v(35.4, -14.29) * mm});
            skLineSegment(sketch, "E12.69.3", {"start": v(36.29, -14.1) * mm, "end": v(35.58, -13.81) * mm});
            skArc(sketch, "E12.70.0", {"start": v(36.94, -12.27) * mm, "mid": v(37.26, -12.1) * mm, "end": v(37.1, -11.79) * mm});
            skLineSegment(sketch, "E12.70.1", {"start": v(36.94, -12.27) * mm, "end": v(36.22, -12.03) * mm});
            skArc(sketch, "E12.70.2", {"start": v(36.37, -11.55) * mm, "mid": v(36.05, -11.71) * mm, "end": v(36.22, -12.03) * mm});
            skLineSegment(sketch, "E12.70.3", {"start": v(37.1, -11.79) * mm, "end": v(36.37, -11.55) * mm});
            skArc(sketch, "E12.71.0", {"start": v(37.64, -9.93) * mm, "mid": v(37.95, -9.74) * mm, "end": v(37.77, -9.43) * mm});
            skLineSegment(sketch, "E12.71.1", {"start": v(37.64, -9.93) * mm, "end": v(36.9, -9.74) * mm});
            skArc(sketch, "E12.71.2", {"start": v(37.03, -9.24) * mm, "mid": v(36.72, -9.43) * mm, "end": v(36.9, -9.74) * mm});
            skLineSegment(sketch, "E12.71.3", {"start": v(37.77, -9.43) * mm, "end": v(37.03, -9.24) * mm});
            skArc(sketch, "E12.72.0", {"start": v(38.19, -7.54) * mm, "mid": v(38.49, -7.34) * mm, "end": v(38.28, -7.04) * mm});
            skLineSegment(sketch, "E12.72.1", {"start": v(38.19, -7.54) * mm, "end": v(37.44, -7.4) * mm});
            skArc(sketch, "E12.72.2", {"start": v(37.54, -6.9) * mm, "mid": v(37.24, -7.1) * mm, "end": v(37.44, -7.4) * mm});
            skLineSegment(sketch, "E12.72.3", {"start": v(38.28, -7.04) * mm, "end": v(37.54, -6.9) * mm});
            skArc(sketch, "E12.73.0", {"start": v(38.59, -5.13) * mm, "mid": v(38.87, -4.91) * mm, "end": v(38.65, -4.63) * mm});
            skLineSegment(sketch, "E12.73.1", {"start": v(38.59, -5.13) * mm, "end": v(37.83, -5.04) * mm});
            skArc(sketch, "E12.73.2", {"start": v(37.9, -4.53) * mm, "mid": v(37.61, -4.75) * mm, "end": v(37.83, -5.04) * mm});
            skLineSegment(sketch, "E12.73.3", {"start": v(38.65, -4.63) * mm, "end": v(37.9, -4.53) * mm});
            skArc(sketch, "E12.74.0", {"start": v(38.83, -2.7) * mm, "mid": v(39.1, -2.46) * mm, "end": v(38.86, -2.2) * mm});
            skLineSegment(sketch, "E12.74.1", {"start": v(38.83, -2.7) * mm, "end": v(38.07, -2.65) * mm});
            skArc(sketch, "E12.74.2", {"start": v(38.1, -2.14) * mm, "mid": v(37.83, -2.38) * mm, "end": v(38.07, -2.65) * mm});
            skLineSegment(sketch, "E12.74.3", {"start": v(38.86, -2.2) * mm, "end": v(38.1, -2.14) * mm});
            skArc(sketch, "E12.75.0", {"start": v(38.93, -0.25) * mm, "mid": v(39.18, 0) * mm, "end": v(38.93, 0.25) * mm});
            skLineSegment(sketch, "E12.75.1", {"start": v(38.93, -0.25) * mm, "end": v(38.16, -0.25) * mm});
            skArc(sketch, "E12.75.2", {"start": v(38.16, 0.25) * mm, "mid": v(37.9, 0) * mm, "end": v(38.16, -0.25) * mm});
            skLineSegment(sketch, "E12.75.3", {"start": v(38.93, 0.25) * mm, "end": v(38.16, 0.25) * mm});
            skArc(sketch, "E12.76.0", {"start": v(38.86, 2.2) * mm, "mid": v(39.1, 2.46) * mm, "end": v(38.83, 2.7) * mm});
            skLineSegment(sketch, "E12.76.1", {"start": v(38.86, 2.2) * mm, "end": v(38.1, 2.14) * mm});
            skArc(sketch, "E12.76.2", {"start": v(38.07, 2.65) * mm, "mid": v(37.83, 2.38) * mm, "end": v(38.1, 2.14) * mm});
            skLineSegment(sketch, "E12.76.3", {"start": v(38.83, 2.7) * mm, "end": v(38.07, 2.65) * mm});
            skArc(sketch, "E12.77.0", {"start": v(38.65, 4.63) * mm, "mid": v(38.87, 4.91) * mm, "end": v(38.59, 5.13) * mm});
            skLineSegment(sketch, "E12.77.1", {"start": v(38.65, 4.63) * mm, "end": v(37.9, 4.53) * mm});
            skArc(sketch, "E12.77.2", {"start": v(37.83, 5.04) * mm, "mid": v(37.61, 4.75) * mm, "end": v(37.9, 4.53) * mm});
            skLineSegment(sketch, "E12.77.3", {"start": v(38.59, 5.13) * mm, "end": v(37.83, 5.04) * mm});
            skArc(sketch, "E12.78.0", {"start": v(38.28, 7.04) * mm, "mid": v(38.49, 7.34) * mm, "end": v(38.19, 7.54) * mm});
            skLineSegment(sketch, "E12.78.1", {"start": v(38.28, 7.04) * mm, "end": v(37.54, 6.9) * mm});
            skArc(sketch, "E12.78.2", {"start": v(37.44, 7.4) * mm, "mid": v(37.24, 7.1) * mm, "end": v(37.54, 6.9) * mm});
            skLineSegment(sketch, "E12.78.3", {"start": v(38.19, 7.54) * mm, "end": v(37.44, 7.4) * mm});
            skArc(sketch, "E12.79.0", {"start": v(37.77, 9.43) * mm, "mid": v(37.95, 9.74) * mm, "end": v(37.64, 9.93) * mm});
            skLineSegment(sketch, "E12.79.1", {"start": v(37.77, 9.43) * mm, "end": v(37.03, 9.24) * mm});
            skArc(sketch, "E12.79.2", {"start": v(36.9, 9.74) * mm, "mid": v(36.72, 9.43) * mm, "end": v(37.03, 9.24) * mm});
            skLineSegment(sketch, "E12.79.3", {"start": v(37.64, 9.93) * mm, "end": v(36.9, 9.74) * mm});
            skArc(sketch, "E12.80.0", {"start": v(37.1, 11.79) * mm, "mid": v(37.26, 12.1) * mm, "end": v(36.94, 12.27) * mm});
            skLineSegment(sketch, "E12.80.1", {"start": v(37.1, 11.79) * mm, "end": v(36.37, 11.55) * mm});
            skArc(sketch, "E12.80.2", {"start": v(36.22, 12.03) * mm, "mid": v(36.05, 11.71) * mm, "end": v(36.37, 11.55) * mm});
            skLineSegment(sketch, "E12.80.3", {"start": v(36.94, 12.27) * mm, "end": v(36.22, 12.03) * mm});
            skArc(sketch, "E12.81.0", {"start": v(36.29, 14.1) * mm, "mid": v(36.43, 14.42) * mm, "end": v(36.1, 14.57) * mm});
            skLineSegment(sketch, "E12.81.1", {"start": v(36.29, 14.1) * mm, "end": v(35.58, 13.81) * mm});
            skArc(sketch, "E12.81.2", {"start": v(35.4, 14.29) * mm, "mid": v(35.25, 13.96) * mm, "end": v(35.58, 13.81) * mm});
            skLineSegment(sketch, "E12.81.3", {"start": v(36.1, 14.57) * mm, "end": v(35.4, 14.29) * mm});
            skArc(sketch, "E12.82.0", {"start": v(35.33, 16.34) * mm, "mid": v(35.45, 16.68) * mm, "end": v(35.11, 16.8) * mm});
            skLineSegment(sketch, "E12.82.1", {"start": v(35.33, 16.34) * mm, "end": v(34.64, 16.02) * mm});
            skArc(sketch, "E12.82.2", {"start": v(34.42, 16.48) * mm, "mid": v(34.3, 16.14) * mm, "end": v(34.64, 16.02) * mm});
            skLineSegment(sketch, "E12.82.3", {"start": v(35.11, 16.8) * mm, "end": v(34.42, 16.48) * mm});
            skArc(sketch, "E12.83.0", {"start": v(34.23, 18.53) * mm, "mid": v(34.33, 18.87) * mm, "end": v(33.99, 18.98) * mm});
            skLineSegment(sketch, "E12.83.1", {"start": v(34.23, 18.53) * mm, "end": v(33.57, 18.16) * mm});
            skArc(sketch, "E12.83.2", {"start": v(33.32, 18.6) * mm, "mid": v(33.22, 18.26) * mm, "end": v(33.57, 18.16) * mm});
            skLineSegment(sketch, "E12.83.3", {"start": v(33.99, 18.98) * mm, "end": v(33.32, 18.6) * mm});
            skArc(sketch, "E12.84.0", {"start": v(33, 20.64) * mm, "mid": v(33.08, 21) * mm, "end": v(32.73, 21.07) * mm});
            skLineSegment(sketch, "E12.84.1", {"start": v(33, 20.64) * mm, "end": v(32.36, 20.23) * mm});
            skArc(sketch, "E12.84.2", {"start": v(32.09, 20.66) * mm, "mid": v(32, 20.31) * mm, "end": v(32.36, 20.23) * mm});
            skLineSegment(sketch, "E12.84.3", {"start": v(32.73, 21.07) * mm, "end": v(32.09, 20.66) * mm});
            skArc(sketch, "E12.85.0", {"start": v(31.64, 22.67) * mm, "mid": v(31.7, 23.03) * mm, "end": v(31.34, 23.09) * mm});
            skLineSegment(sketch, "E12.85.1", {"start": v(31.64, 22.67) * mm, "end": v(31.02, 22.23) * mm});
            skArc(sketch, "E12.85.2", {"start": v(30.73, 22.64) * mm, "mid": v(30.67, 22.28) * mm, "end": v(31.02, 22.23) * mm});
            skLineSegment(sketch, "E12.85.3", {"start": v(31.34, 23.09) * mm, "end": v(30.73, 22.64) * mm});
            skArc(sketch, "E12.86.0", {"start": v(30.15, 24.62) * mm, "mid": v(30.19, 24.97) * mm, "end": v(29.83, 25) * mm});
            skLineSegment(sketch, "E12.86.1", {"start": v(30.15, 24.62) * mm, "end": v(29.57, 24.13) * mm});
            skArc(sketch, "E12.86.2", {"start": v(29.24, 24.52) * mm, "mid": v(29.2, 24.16) * mm, "end": v(29.57, 24.13) * mm});
            skLineSegment(sketch, "E12.86.3", {"start": v(29.83, 25) * mm, "end": v(29.24, 24.52) * mm});
            skArc(sketch, "E12.87.0", {"start": v(28.55, 26.46) * mm, "mid": v(28.56, 26.82) * mm, "end": v(28.2, 26.83) * mm});
            skLineSegment(sketch, "E12.87.1", {"start": v(28.55, 26.46) * mm, "end": v(28, 25.94) * mm});
            skArc(sketch, "E12.87.2", {"start": v(27.65, 26.3) * mm, "mid": v(27.63, 25.95) * mm, "end": v(28, 25.94) * mm});
            skLineSegment(sketch, "E12.87.3", {"start": v(28.2, 26.83) * mm, "end": v(27.65, 26.3) * mm});
            skArc(sketch, "E12.88.0", {"start": v(26.83, 28.2) * mm, "mid": v(26.82, 28.56) * mm, "end": v(26.46, 28.55) * mm});
            skLineSegment(sketch, "E12.88.1", {"start": v(26.83, 28.2) * mm, "end": v(26.3, 27.65) * mm});
            skArc(sketch, "E12.88.2", {"start": v(25.94, 28) * mm, "mid": v(25.95, 27.63) * mm, "end": v(26.3, 27.65) * mm});
            skLineSegment(sketch, "E12.88.3", {"start": v(26.46, 28.55) * mm, "end": v(25.94, 28) * mm});
            skArc(sketch, "E12.89.0", {"start": v(25, 29.83) * mm, "mid": v(24.97, 30.19) * mm, "end": v(24.62, 30.15) * mm});
            skLineSegment(sketch, "E12.89.1", {"start": v(25, 29.83) * mm, "end": v(24.52, 29.24) * mm});
            skArc(sketch, "E12.89.2", {"start": v(24.13, 29.57) * mm, "mid": v(24.16, 29.2) * mm, "end": v(24.52, 29.24) * mm});
            skLineSegment(sketch, "E12.89.3", {"start": v(24.62, 30.15) * mm, "end": v(24.13, 29.57) * mm});
            skArc(sketch, "E12.90.0", {"start": v(23.09, 31.34) * mm, "mid": v(23.03, 31.7) * mm, "end": v(22.67, 31.64) * mm});
            skLineSegment(sketch, "E12.90.1", {"start": v(23.09, 31.34) * mm, "end": v(22.64, 30.73) * mm});
            skArc(sketch, "E12.90.2", {"start": v(22.23, 31.02) * mm, "mid": v(22.28, 30.67) * mm, "end": v(22.64, 30.73) * mm});
            skLineSegment(sketch, "E12.90.3", {"start": v(22.67, 31.64) * mm, "end": v(22.23, 31.02) * mm});
            skArc(sketch, "E12.91.0", {"start": v(21.07, 32.73) * mm, "mid": v(21, 33.08) * mm, "end": v(20.64, 33) * mm});
            skLineSegment(sketch, "E12.91.1", {"start": v(21.07, 32.73) * mm, "end": v(20.66, 32.09) * mm});
            skArc(sketch, "E12.91.2", {"start": v(20.23, 32.36) * mm, "mid": v(20.31, 32) * mm, "end": v(20.66, 32.09) * mm});
            skLineSegment(sketch, "E12.91.3", {"start": v(20.64, 33) * mm, "end": v(20.23, 32.36) * mm});
            skArc(sketch, "E12.92.0", {"start": v(18.98, 33.99) * mm, "mid": v(18.87, 34.33) * mm, "end": v(18.53, 34.23) * mm});
            skLineSegment(sketch, "E12.92.1", {"start": v(18.98, 33.99) * mm, "end": v(18.6, 33.32) * mm});
            skArc(sketch, "E12.92.2", {"start": v(18.16, 33.57) * mm, "mid": v(18.26, 33.22) * mm, "end": v(18.6, 33.32) * mm});
            skLineSegment(sketch, "E12.92.3", {"start": v(18.53, 34.23) * mm, "end": v(18.16, 33.57) * mm});
            skArc(sketch, "E12.93.0", {"start": v(16.8, 35.11) * mm, "mid": v(16.68, 35.45) * mm, "end": v(16.34, 35.33) * mm});
            skLineSegment(sketch, "E12.93.1", {"start": v(16.8, 35.11) * mm, "end": v(16.48, 34.42) * mm});
            skArc(sketch, "E12.93.2", {"start": v(16.02, 34.64) * mm, "mid": v(16.14, 34.3) * mm, "end": v(16.48, 34.42) * mm});
            skLineSegment(sketch, "E12.93.3", {"start": v(16.34, 35.33) * mm, "end": v(16.02, 34.64) * mm});
            skArc(sketch, "E12.94.0", {"start": v(14.57, 36.1) * mm, "mid": v(14.42, 36.43) * mm, "end": v(14.1, 36.29) * mm});
            skLineSegment(sketch, "E12.94.1", {"start": v(14.57, 36.1) * mm, "end": v(14.29, 35.4) * mm});
            skArc(sketch, "E12.94.2", {"start": v(13.81, 35.58) * mm, "mid": v(13.96, 35.25) * mm, "end": v(14.29, 35.4) * mm});
            skLineSegment(sketch, "E12.94.3", {"start": v(14.1, 36.29) * mm, "end": v(13.81, 35.58) * mm});
            skArc(sketch, "E12.95.0", {"start": v(12.27, 36.94) * mm, "mid": v(12.1, 37.26) * mm, "end": v(11.79, 37.1) * mm});
            skLineSegment(sketch, "E12.95.1", {"start": v(12.27, 36.94) * mm, "end": v(12.03, 36.22) * mm});
            skArc(sketch, "E12.95.2", {"start": v(11.55, 36.37) * mm, "mid": v(11.71, 36.05) * mm, "end": v(12.03, 36.22) * mm});
            skLineSegment(sketch, "E12.95.3", {"start": v(11.79, 37.1) * mm, "end": v(11.55, 36.37) * mm});
            skArc(sketch, "E12.96.0", {"start": v(9.93, 37.64) * mm, "mid": v(9.74, 37.95) * mm, "end": v(9.43, 37.77) * mm});
            skLineSegment(sketch, "E12.96.1", {"start": v(9.93, 37.64) * mm, "end": v(9.74, 36.9) * mm});
            skArc(sketch, "E12.96.2", {"start": v(9.24, 37.03) * mm, "mid": v(9.43, 36.72) * mm, "end": v(9.74, 36.9) * mm});
            skLineSegment(sketch, "E12.96.3", {"start": v(9.43, 37.77) * mm, "end": v(9.24, 37.03) * mm});
            skArc(sketch, "E12.97.0", {"start": v(7.54, 38.19) * mm, "mid": v(7.34, 38.49) * mm, "end": v(7.04, 38.28) * mm});
            skLineSegment(sketch, "E12.97.1", {"start": v(7.54, 38.19) * mm, "end": v(7.4, 37.44) * mm});
            skArc(sketch, "E12.97.2", {"start": v(6.9, 37.54) * mm, "mid": v(7.1, 37.24) * mm, "end": v(7.4, 37.44) * mm});
            skLineSegment(sketch, "E12.97.3", {"start": v(7.04, 38.28) * mm, "end": v(6.9, 37.54) * mm});
            skArc(sketch, "E12.98.0", {"start": v(5.13, 38.59) * mm, "mid": v(4.91, 38.87) * mm, "end": v(4.63, 38.65) * mm});
            skLineSegment(sketch, "E12.98.1", {"start": v(5.13, 38.59) * mm, "end": v(5.04, 37.83) * mm});
            skArc(sketch, "E12.98.2", {"start": v(4.53, 37.9) * mm, "mid": v(4.75, 37.61) * mm, "end": v(5.04, 37.83) * mm});
            skLineSegment(sketch, "E12.98.3", {"start": v(4.63, 38.65) * mm, "end": v(4.53, 37.9) * mm});
            skArc(sketch, "E12.99.0", {"start": v(2.7, 38.83) * mm, "mid": v(2.46, 39.1) * mm, "end": v(2.2, 38.86) * mm});
            skLineSegment(sketch, "E12.99.1", {"start": v(2.7, 38.83) * mm, "end": v(2.65, 38.07) * mm});
            skArc(sketch, "E12.99.2", {"start": v(2.14, 38.1) * mm, "mid": v(2.38, 37.83) * mm, "end": v(2.65, 38.07) * mm});
            skLineSegment(sketch, "E12.99.3", {"start": v(2.2, 38.86) * mm, "end": v(2.14, 38.1) * mm});
            skSolve(sketch);
        }
        {
            var Q0;
            Q0 = qSketchRegion(id + "F7", true);
            extrude(context, id + "F8", {"entities" : qUnion([Q0]), "operationType" : NewBodyOperationType.REMOVE, "endBound" : BoundingType.THROUGH_ALL, "oppositeDirection" : true, "depth" : 25.4 * mm, "offsetDistance" : 25.4 * mm});
        }
    });
